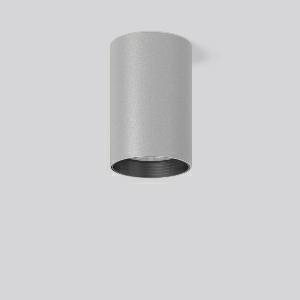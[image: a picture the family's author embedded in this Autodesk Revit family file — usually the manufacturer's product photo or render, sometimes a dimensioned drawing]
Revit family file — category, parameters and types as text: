
# Revit family: heledon_maxi_a_931222_004_a03c
name_source: partatom
category: Lighting Fixtures
units: mm (PartAtom-declared; Revit-internal decimal feet)

## family parameters
Cut with Voids When Loaded = No
Host = Face
Light Source = No
Part Type = Normal
Room Calculation Point = No
Round Connector Dimension = Use Diameter
Shared = No

## types (1)
- HELEDON maxi A (1 x LED Modul 930, 2800 lm, 3000)
    Apparent Load = 25 VA
    Approval mark = CE
    CIE Flux Codes = 96 100 100 100 100
    Color Rendering = 90
    Color Temperature = 3000
    Default Elevation = 1800 mm
    Description = Series: HELEDON maxi
Cylindrical surface-mounted downlight. Housing: die-cast aluminium, powder-coated. Internal ceiling frame polycarbonate with bayonet mounting. Black plastic ring and recessed LED to prevent glare from the side. Optical assembly with lens made of plastic (polycarbonate) for the best homogeneous light distribution - can be changed without tools. Best colour rendering index Ra>90. Suitable for Ceiling mounting. Easy installation with a separate ceiling frame with bayonet mounting and plug connection. Driver integrated. Connected via plug-in connector. High quality converter without flickering and stroboscopic effect. The following accessories can be mounted without use of tools: interchangeable lenses, decorative glasses, honeycomb louvre, clear and frosted diffusers, white interchangeable plastic ring. 
Colour: silver
Diameter: 123 mm
Height: 183 mm
Lamp: LED
Socket: without socket
Colour temperature: 3000K
Colour rendering index (CRI): 92
System power: 25 W
Rated luminous flux: 2800 lm
Luminous efficiency: 112 lm/W
Control gear: Regulated power supply
Protection class: I
Type of protection: IP 20
    Height = 183 mm
    Lamp = 1 x LED Modul 930
    Lamp Light Flux = 2800 lm
    Lamp count = 1
    Length = 123 mm
    Lifetime = 50000 h
    Luminous efficacy = 112 lm/W
    Manufacturer = RZB
    ModVariant = No
    Model = 931222.004
    Mounting Place = Ceiling
    Mounting Type = Surface mounted
    Number of Poles = 1
    OnlyDefault = Yes
    Power Factor = 1
    Product Name = HELEDON maxi A
    Product group = Surface mounted downlights
    ProductGroupID = 302
    Protection Class = Protection class I
    Protection Degree = IP 20
    RLX_Detail_Level = 1
    RLX_Emergency_Light_Flux = 0 lm
    RLX_Emergency_Type = 0
    RLX_Emergency_Type_DB = No
    RlxData = <blob elided: 100425 chars, md5=6c4dd919>
    Socket = socket
    Standby Power = 0 W
    System Light Flux = 2800 lm
    System Power = 25 W
    Type Comments = Product without accessories
    Type Image = 931193.004.jpg
    URL = http://relux.com
    VarID = ---
    Voltage = 230 V
    Voltage Range = 220-240 V
    Weight = 0.00 kg
    Width = 0 mm  [stored 0 ft]

note: [stored X ft] marks values corroborated as IEEE doubles in the binary element streams (Revit-internal decimal feet)

## geometry (parser evidence)
native form markers: Blend x4, Sweep x10
no freeform markers — native parametric forms only
